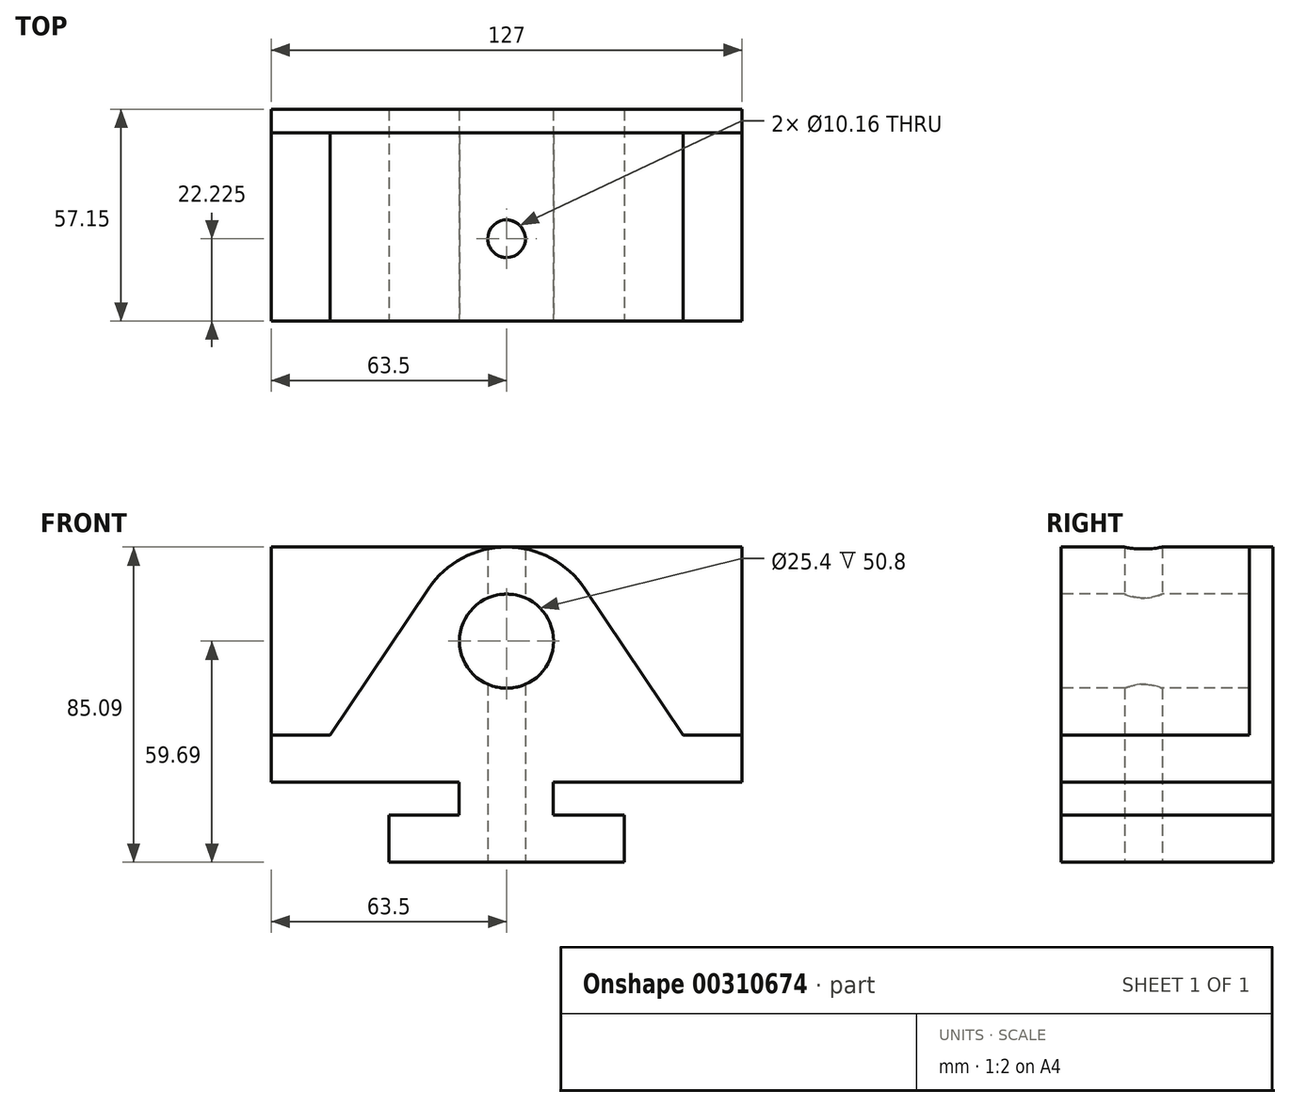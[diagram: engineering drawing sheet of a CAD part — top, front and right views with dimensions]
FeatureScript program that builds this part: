
annotation { "Feature Type Name" : "Feature", "Feature Type Description" : "" }
export const myFeature = defineFeature(function(context is Context, id is Id, definition is map)
    precondition{}
    {
        {
            var Q0;
            Q0=qCreatedBy(makeId("Top.planeOp"),FACE);
            var sketch = newSketch(context, id + "F0", { "sketchPlane" : qUnion([Q0])});
            skLineSegment(sketch, "E0", {"start": v(-63.5, 0) * mm, "end": v(63.5, 0) * mm});
            skLineSegment(sketch, "E1", {"start": v(63.5, 0) * mm, "end": v(63.5, 57.15) * mm});
            skLineSegment(sketch, "E2", {"start": v(63.5, 57.15) * mm, "end": v(-63.5, 57.15) * mm});
            skLineSegment(sketch, "E3", {"start": v(-63.5, 57.15) * mm, "end": v(-63.5, 0) * mm});
            skLineSegment(sketch, "E4", {"start": v(0, 0) * mm, "end": v(0, 44.45) * mm, "construction": true});
            skPoint(sketch, "E4.endSnap0", {"position": v(0, 57.15) * mm});
            skLineSegment(sketch, "E5", {"start": v(-63.5, 44.45) * mm, "end": v(63.5, 44.45) * mm});
            skLineSegment(sketch, "E6", {"start": v(-48.68, 44.45) * mm, "end": v(-48.68, 0) * mm});
            skLineSegment(sketch, "E7", {"start": v(46.57, 44.45) * mm, "end": v(46.57, 0) * mm});
            skCircle(sketch, "E8", {"center": v(0, 22.22) * mm, "radius": 5.08 * mm});
            skSolve(sketch);
        }
        {
            var Q0;
            Q0 = qSketchRegion(id + "F0", true);
            extrude(context, id + "F1", {"entities" : qUnion([Q0]), "depth" : 85.1 * mm});
        }
        {
            var Q0;
            Q0=makeQuery(id+"F1.opExtrude","SWEPT_FACE",FACE,{"disambiguationData":[OSD([sQuery(id+"F0.wireOp",EDGE,"E0")])]});
            var sketch = newSketch(context, id + "F2", { "sketchPlane" : qUnion([Q0])});
            skLineSegment(sketch, "E9", {"start": v(0, 0) * mm, "end": v(0, 85.1) * mm, "construction": true});
            skLineSegment(sketch, "E10", {"start": v(31.75, 0) * mm, "end": v(31.75, 12.7) * mm});
            skLineSegment(sketch, "E11", {"start": v(31.75, 12.7) * mm, "end": v(12.6, 12.7) * mm});
            skLineSegment(sketch, "E12", {"start": v(12.6, 12.7) * mm, "end": v(12.6, 21.59) * mm});
            skLineSegment(sketch, "E13", {"start": v(12.6, 21.59) * mm, "end": v(63.5, 21.59) * mm});
            skLineSegment(sketch, "E14", {"start": v(63.5, 21.59) * mm, "end": v(63.5, 85.1) * mm});
            skLineSegment(sketch, "E15", {"start": v(63.5, 85.1) * mm, "end": v(-63.5, 85.1) * mm});
            skLineSegment(sketch, "E16", {"start": v(-63.5, 85.1) * mm, "end": v(-63.5, 21.59) * mm});
            skLineSegment(sketch, "E17", {"start": v(-63.5, 21.59) * mm, "end": v(-12.8, 21.6) * mm});
            skLineSegment(sketch, "E18", {"start": v(-12.8, 21.6) * mm, "end": v(-12.8, 12.7) * mm});
            skLineSegment(sketch, "E19", {"start": v(-12.8, 12.7) * mm, "end": v(-31.75, 12.7) * mm});
            skLineSegment(sketch, "E20", {"start": v(-31.75, 12.7) * mm, "end": v(-31.75, 0) * mm});
            skLineSegment(sketch, "E21", {"start": v(-31.75, 0) * mm, "end": v(31.75, 0) * mm});
            skLineSegment(sketch, "E22", {"start": v(-63.5, 34.3) * mm, "end": v(-47.63, 34.3) * mm});
            skLineSegment(sketch, "E23", {"start": v(-47.63, 34.3) * mm, "end": v(-21.1, 73.84) * mm});
            skLineSegment(sketch, "E24", {"start": v(21.1, 73.84) * mm, "end": v(47.63, 34.29) * mm});
            skLineSegment(sketch, "E25", {"start": v(47.63, 34.3) * mm, "end": v(63.5, 34.3) * mm});
            skArc(sketch, "E26", {"start": v(21.1, 73.84) * mm, "mid": v(0, 85.1) * mm, "end": v(-21.1, 73.84) * mm});
            skCircle(sketch, "E27", {"center": v(0, 59.7) * mm, "radius": 12.7 * mm});
            skSolve(sketch);
        }
        {
            var Q0;
            Q0=makeQuery(id+"F2.imprint","IMPRINT",FACE,{"disambiguationData":[TD([[makeQuery(id+"F2.imprint","IMPRINT",EDGE,{"derivedFrom":sQuery(id+"F2.wireOp",EDGE,"E27")}),1.0]])]});
            extrude(context, id + "F3", {"entities" : qUnion([Q0]), "operationType" : NewBodyOperationType.REMOVE, "oppositeDirection" : true, "depth" : 50.8 * mm});
        }
        {
            var Q0;
            {var subQ0=sQuery(id+"F2.wireOp",EDGE,"E22");Q0=makeQuery(id+"F2.imprint","IMPRINT",FACE,{"disambiguationData":[TD([[makeQuery(id+"F2.imprint","IMPRINT",EDGE,{"derivedFrom":subQ0}),1.0]])]});}
            var Q1;
            {var subQ6=sQuery(id+"F2.wireOp",EDGE,"E24");Q1=makeQuery(id+"F2.imprint","IMPRINT",FACE,{"disambiguationData":[TD([[makeQuery(id+"F2.imprint","IMPRINT",EDGE,{"derivedFrom":subQ6}),1.0]])]});}
            extrude(context, id + "F4", {"entities" : qUnion([Q0, Q1]), "operationType" : NewBodyOperationType.REMOVE, "oppositeDirection" : true, "depth" : 50.8 * mm});
        }
        {
            var Q0;
            {var subQ5=sQuery(id+"F2.wireOp",EDGE,"E17");Q0=makeQuery(id+"F2.imprint","IMPRINT",FACE,{"disambiguationData":[TD([[makeQuery(id+"F2.imprint","IMPRINT",EDGE,{"derivedFrom":subQ5}),-1.0]])]});}
            var Q1;
            {var subQ5=sQuery(id+"F2.wireOp",EDGE,"E10");Q1=makeQuery(id+"F2.imprint","IMPRINT",FACE,{"disambiguationData":[TD([[makeQuery(id+"F2.imprint","IMPRINT",EDGE,{"derivedFrom":subQ5}),-1.0]])]});}
            extrude(context, id + "F5", {"entities" : qUnion([Q0, Q1]), "operationType" : NewBodyOperationType.REMOVE, "endBound" : BoundingType.THROUGH_ALL, "oppositeDirection" : true, "depth" : 50.8 * mm});
        }
    });
